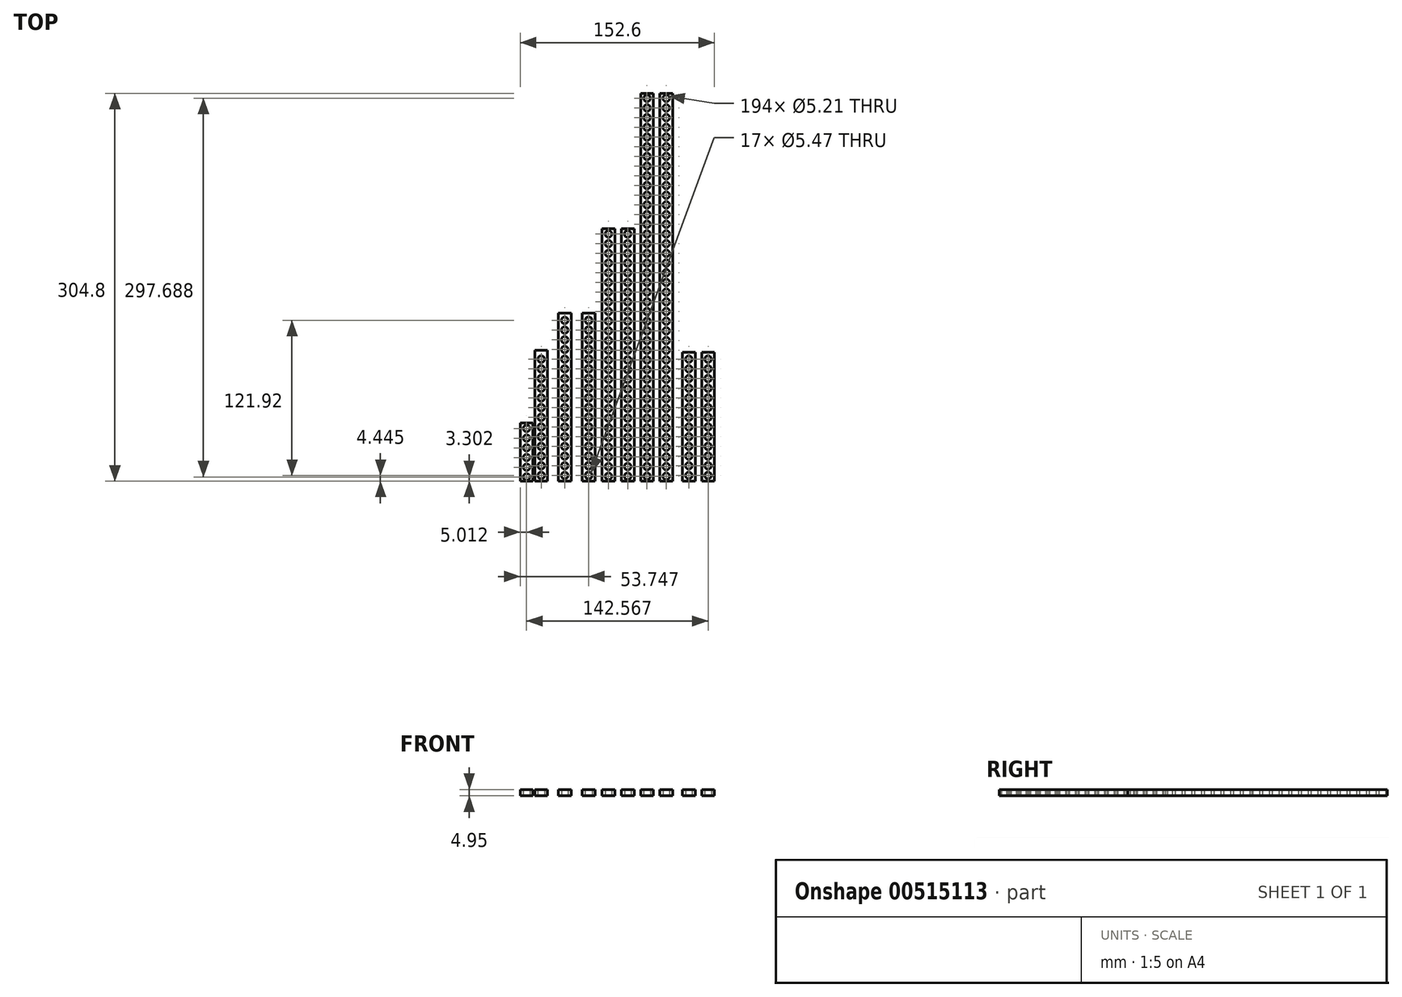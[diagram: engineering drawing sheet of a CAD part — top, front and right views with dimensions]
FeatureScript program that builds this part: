
annotation { "Feature Type Name" : "Feature", "Feature Type Description" : "" }
export const myFeature = defineFeature(function(context is Context, id is Id, definition is map)
    precondition{}
    {
        {
            var Q0;
            Q0=qCreatedBy(makeId("Top.planeOp"),FACE);
            var sketch = newSketch(context, id + "F0", { "sketchPlane" : qUnion([Q0])});
            skLineSegment(sketch, "E0.bottom", {"start": v(-63.67, 0) * mm, "end": v(-53.64, 0) * mm});
            skLineSegment(sketch, "E0.top", {"start": v(-63.67, 102.87) * mm, "end": v(-53.64, 102.87) * mm});
            skLineSegment(sketch, "E0.left", {"start": v(-63.67, 0) * mm, "end": v(-63.67, 102.87) * mm});
            skLineSegment(sketch, "E0.right", {"start": v(-53.64, 0) * mm, "end": v(-53.64, 102.87) * mm});
            skCircle(sketch, "E1", {"center": v(-58.66, 4.45) * mm, "radius": 2.6 * mm});
            skPoint(sketch, "E1.centerSnap0", {"position": v(-58.66, 0) * mm});
            skCircle(sketch, "E2.0.1.0", {"center": v(-58.66, 12.06) * mm, "radius": 2.6 * mm});
            skCircle(sketch, "E2.0.2.0", {"center": v(-58.66, 19.69) * mm, "radius": 2.6 * mm});
            skCircle(sketch, "E2.0.3.0", {"center": v(-58.66, 27.3) * mm, "radius": 2.6 * mm});
            skCircle(sketch, "E2.0.4.0", {"center": v(-58.66, 34.92) * mm, "radius": 2.6 * mm});
            skCircle(sketch, "E2.0.5.0", {"center": v(-58.66, 42.55) * mm, "radius": 2.6 * mm});
            skCircle(sketch, "E2.0.6.0", {"center": v(-58.66, 50.16) * mm, "radius": 2.6 * mm});
            skCircle(sketch, "E2.0.7.0", {"center": v(-58.66, 57.78) * mm, "radius": 2.6 * mm});
            skCircle(sketch, "E2.0.8.0", {"center": v(-58.66, 65.4) * mm, "radius": 2.6 * mm});
            skCircle(sketch, "E2.0.9.0", {"center": v(-58.66, 73.03) * mm, "radius": 2.6 * mm});
            skCircle(sketch, "E2.0.10.0", {"center": v(-58.66, 80.65) * mm, "radius": 2.6 * mm});
            skCircle(sketch, "E2.0.11.0", {"center": v(-58.66, 88.27) * mm, "radius": 2.6 * mm});
            skCircle(sketch, "E2.0.12.0", {"center": v(-58.66, 95.88) * mm, "radius": 2.6 * mm});
            skLineSegment(sketch, "E2.direction1", {"start": v(-58.66, 4.44) * mm, "end": v(-33.26, 4.45) * mm, "construction": true});
            skLineSegment(sketch, "E2.direction2", {"start": v(-58.66, 4.45) * mm, "end": v(-58.66, 12.06) * mm, "construction": true});
            skSolve(sketch);
        }
        {
            var Q0;
            Q0=makeQuery(id+"F0.imprint","IMPRINT",FACE,{"disambiguationData":[TD([[makeQuery(id+"F0.imprint","IMPRINT",EDGE,{"derivedFrom":sQuery(id+"F0.wireOp",EDGE,"E0.bottom")}),1.0]])]});
            extrude(context, id + "F1", {"entities" : qUnion([Q0]), "depth" : 4.95 * mm, "offsetDistance" : 25.4 * mm});
        }
        {
            var Q0;
            Q0=qCreatedBy(makeId("Top.planeOp"),FACE);
            var sketch = newSketch(context, id + "F2", { "sketchPlane" : qUnion([Q0])});
            skLineSegment(sketch, "E3.bottom", {"start": v(-45.23, 0) * mm, "end": v(-35.2, 0) * mm});
            skLineSegment(sketch, "E3.top", {"start": v(-45.23, 132.08) * mm, "end": v(-35.2, 132.08) * mm});
            skLineSegment(sketch, "E3.left", {"start": v(-45.23, 0) * mm, "end": v(-45.23, 132.08) * mm});
            skLineSegment(sketch, "E3.right", {"start": v(-35.2, 0) * mm, "end": v(-35.2, 132.08) * mm});
            skCircle(sketch, "E4", {"center": v(-40.2, 4.44) * mm, "radius": 2.6 * mm});
            skPoint(sketch, "E4.centerSnap0", {"position": v(-40.2, 0) * mm});
            skCircle(sketch, "E5.0.1.0", {"center": v(-40.2, 12.06) * mm, "radius": 2.6 * mm});
            skCircle(sketch, "E5.0.2.0", {"center": v(-40.2, 19.69) * mm, "radius": 2.6 * mm});
            skCircle(sketch, "E5.0.3.0", {"center": v(-40.2, 27.3) * mm, "radius": 2.6 * mm});
            skCircle(sketch, "E5.0.4.0", {"center": v(-40.2, 34.92) * mm, "radius": 2.6 * mm});
            skCircle(sketch, "E5.0.5.0", {"center": v(-40.2, 42.55) * mm, "radius": 2.6 * mm});
            skCircle(sketch, "E5.0.6.0", {"center": v(-40.2, 50.16) * mm, "radius": 2.6 * mm});
            skCircle(sketch, "E5.0.7.0", {"center": v(-40.2, 57.78) * mm, "radius": 2.6 * mm});
            skCircle(sketch, "E5.0.8.0", {"center": v(-40.2, 65.4) * mm, "radius": 2.6 * mm});
            skCircle(sketch, "E5.0.9.0", {"center": v(-40.2, 73.03) * mm, "radius": 2.6 * mm});
            skCircle(sketch, "E5.0.10.0", {"center": v(-40.2, 80.65) * mm, "radius": 2.6 * mm});
            skCircle(sketch, "E5.0.11.0", {"center": v(-40.2, 88.27) * mm, "radius": 2.6 * mm});
            skCircle(sketch, "E5.0.12.0", {"center": v(-40.2, 95.88) * mm, "radius": 2.6 * mm});
            skCircle(sketch, "E5.0.13.0", {"center": v(-40.2, 103.5) * mm, "radius": 2.6 * mm});
            skCircle(sketch, "E5.0.14.0", {"center": v(-40.2, 111.12) * mm, "radius": 2.6 * mm});
            skCircle(sketch, "E5.0.15.0", {"center": v(-40.2, 118.75) * mm, "radius": 2.6 * mm});
            skCircle(sketch, "E5.0.16.0", {"center": v(-40.2, 126.37) * mm, "radius": 2.6 * mm});
            skLineSegment(sketch, "E5.direction1", {"start": v(-40.2, 4.44) * mm, "end": v(-14.8, 4.45) * mm, "construction": true});
            skLineSegment(sketch, "E5.direction2", {"start": v(-40.2, 4.44) * mm, "end": v(-40.2, 12.06) * mm, "construction": true});
            skSolve(sketch);
        }
        {
            var Q0;
            Q0=makeQuery(id+"F2.imprint","IMPRINT",FACE,{"disambiguationData":[TD([[makeQuery(id+"F2.imprint","IMPRINT",EDGE,{"derivedFrom":sQuery(id+"F2.wireOp",EDGE,"E3.bottom")}),1.0]])]});
            extrude(context, id + "F3", {"entities" : qUnion([Q0]), "depth" : 4.95 * mm, "offsetDistance" : 25.4 * mm});
        }
        {
            var Q0;
            Q0=qCreatedBy(makeId("Top.planeOp"),FACE);
            var sketch = newSketch(context, id + "F4", { "sketchPlane" : qUnion([Q0])});
            skLineSegment(sketch, "E6.bottom", {"start": v(-26.44, 0) * mm, "end": v(-16.4, 0) * mm});
            skLineSegment(sketch, "E6.top", {"start": v(-26.44, 132.08) * mm, "end": v(-16.4, 132.08) * mm});
            skLineSegment(sketch, "E6.left", {"start": v(-26.44, 0) * mm, "end": v(-26.44, 132.08) * mm});
            skLineSegment(sketch, "E6.right", {"start": v(-16.4, 0) * mm, "end": v(-16.4, 132.08) * mm});
            skCircle(sketch, "E7", {"center": v(-21.42, 4.45) * mm, "radius": 2.73 * mm});
            skPoint(sketch, "E7.centerSnap0", {"position": v(-21.42, 0) * mm});
            skCircle(sketch, "E8.0.1.0", {"center": v(-21.42, 12.06) * mm, "radius": 2.73 * mm});
            skCircle(sketch, "E8.0.2.0", {"center": v(-21.42, 19.69) * mm, "radius": 2.73 * mm});
            skCircle(sketch, "E8.0.3.0", {"center": v(-21.42, 27.3) * mm, "radius": 2.73 * mm});
            skCircle(sketch, "E8.0.4.0", {"center": v(-21.42, 34.92) * mm, "radius": 2.73 * mm});
            skCircle(sketch, "E8.0.5.0", {"center": v(-21.42, 42.55) * mm, "radius": 2.73 * mm});
            skCircle(sketch, "E8.0.6.0", {"center": v(-21.42, 50.16) * mm, "radius": 2.73 * mm});
            skCircle(sketch, "E8.0.7.0", {"center": v(-21.42, 57.78) * mm, "radius": 2.73 * mm});
            skCircle(sketch, "E8.0.8.0", {"center": v(-21.42, 65.4) * mm, "radius": 2.73 * mm});
            skCircle(sketch, "E8.0.9.0", {"center": v(-21.42, 73.03) * mm, "radius": 2.73 * mm});
            skCircle(sketch, "E8.0.10.0", {"center": v(-21.42, 80.65) * mm, "radius": 2.73 * mm});
            skCircle(sketch, "E8.0.11.0", {"center": v(-21.42, 88.27) * mm, "radius": 2.73 * mm});
            skCircle(sketch, "E8.0.12.0", {"center": v(-21.42, 95.88) * mm, "radius": 2.73 * mm});
            skCircle(sketch, "E8.0.13.0", {"center": v(-21.42, 103.5) * mm, "radius": 2.73 * mm});
            skCircle(sketch, "E8.0.14.0", {"center": v(-21.42, 111.12) * mm, "radius": 2.73 * mm});
            skCircle(sketch, "E8.0.15.0", {"center": v(-21.42, 118.75) * mm, "radius": 2.73 * mm});
            skCircle(sketch, "E8.0.16.0", {"center": v(-21.42, 126.37) * mm, "radius": 2.73 * mm});
            skLineSegment(sketch, "E8.direction1", {"start": v(-21.42, 4.45) * mm, "end": v(3.98, 4.45) * mm, "construction": true});
            skLineSegment(sketch, "E8.direction2", {"start": v(-21.42, 4.45) * mm, "end": v(-21.42, 12.06) * mm, "construction": true});
            skSolve(sketch);
        }
        {
            var Q0;
            Q0=makeQuery(id+"F4.imprint","IMPRINT",FACE,{"disambiguationData":[TD([[makeQuery(id+"F4.imprint","IMPRINT",EDGE,{"derivedFrom":sQuery(id+"F4.wireOp",EDGE,"E6.bottom")}),1.0]])]});
            extrude(context, id + "F5", {"entities" : qUnion([Q0]), "depth" : 4.95 * mm, "offsetDistance" : 25.4 * mm});
        }
        {
            var Q0;
            Q0=qCreatedBy(makeId("Top.planeOp"),FACE);
            var sketch = newSketch(context, id + "F6", { "sketchPlane" : qUnion([Q0])});
            skLineSegment(sketch, "E9.bottom", {"start": v(-10.83, 0) * mm, "end": v(-0.8, 0) * mm});
            skLineSegment(sketch, "E9.top", {"start": v(-10.83, 198.44) * mm, "end": v(-0.8, 198.44) * mm});
            skLineSegment(sketch, "E9.left", {"start": v(-10.83, 0) * mm, "end": v(-10.83, 198.44) * mm});
            skLineSegment(sketch, "E9.right", {"start": v(-0.8, 0) * mm, "end": v(-0.8, 198.44) * mm});
            skLineSegment(sketch, "E10.bottom", {"start": v(4.28, 0) * mm, "end": v(14.32, 0) * mm});
            skLineSegment(sketch, "E10.top", {"start": v(4.28, 198.44) * mm, "end": v(14.32, 198.44) * mm});
            skLineSegment(sketch, "E10.left", {"start": v(4.28, 0) * mm, "end": v(4.28, 198.44) * mm});
            skLineSegment(sketch, "E10.right", {"start": v(14.32, 0) * mm, "end": v(14.32, 198.44) * mm});
            skCircle(sketch, "E11", {"center": v(-5.81, 3.81) * mm, "radius": 2.6 * mm});
            skPoint(sketch, "E11.centerSnap0", {"position": v(-5.81, 0) * mm});
            skCircle(sketch, "E12.0.1.0", {"center": v(-5.81, 11.43) * mm, "radius": 2.6 * mm});
            skCircle(sketch, "E12.0.2.0", {"center": v(-5.81, 19.05) * mm, "radius": 2.6 * mm});
            skCircle(sketch, "E12.0.3.0", {"center": v(-5.81, 26.67) * mm, "radius": 2.6 * mm});
            skCircle(sketch, "E12.0.4.0", {"center": v(-5.81, 34.3) * mm, "radius": 2.6 * mm});
            skCircle(sketch, "E12.0.5.0", {"center": v(-5.81, 41.91) * mm, "radius": 2.6 * mm});
            skCircle(sketch, "E12.0.6.0", {"center": v(-5.81, 49.53) * mm, "radius": 2.6 * mm});
            skCircle(sketch, "E12.0.7.0", {"center": v(-5.81, 57.15) * mm, "radius": 2.6 * mm});
            skCircle(sketch, "E12.0.8.0", {"center": v(-5.81, 64.77) * mm, "radius": 2.6 * mm});
            skCircle(sketch, "E12.0.9.0", {"center": v(-5.81, 72.39) * mm, "radius": 2.6 * mm});
            skCircle(sketch, "E12.0.10.0", {"center": v(-5.81, 80) * mm, "radius": 2.6 * mm});
            skCircle(sketch, "E12.0.11.0", {"center": v(-5.81, 87.63) * mm, "radius": 2.6 * mm});
            skCircle(sketch, "E12.0.12.0", {"center": v(-5.81, 95.25) * mm, "radius": 2.6 * mm});
            skCircle(sketch, "E12.0.13.0", {"center": v(-5.81, 102.87) * mm, "radius": 2.6 * mm});
            skCircle(sketch, "E12.0.14.0", {"center": v(-5.81, 110.49) * mm, "radius": 2.6 * mm});
            skCircle(sketch, "E12.0.15.0", {"center": v(-5.81, 118.11) * mm, "radius": 2.6 * mm});
            skCircle(sketch, "E12.0.16.0", {"center": v(-5.81, 125.73) * mm, "radius": 2.6 * mm});
            skCircle(sketch, "E12.0.17.0", {"center": v(-5.81, 133.35) * mm, "radius": 2.6 * mm});
            skCircle(sketch, "E12.0.18.0", {"center": v(-5.81, 140.97) * mm, "radius": 2.6 * mm});
            skCircle(sketch, "E12.0.19.0", {"center": v(-5.81, 148.6) * mm, "radius": 2.6 * mm});
            skCircle(sketch, "E12.0.20.0", {"center": v(-5.81, 156.21) * mm, "radius": 2.6 * mm});
            skCircle(sketch, "E12.0.21.0", {"center": v(-5.81, 163.83) * mm, "radius": 2.6 * mm});
            skCircle(sketch, "E12.0.22.0", {"center": v(-5.81, 171.45) * mm, "radius": 2.6 * mm});
            skCircle(sketch, "E12.0.23.0", {"center": v(-5.81, 179.07) * mm, "radius": 2.6 * mm});
            skCircle(sketch, "E12.0.24.0", {"center": v(-5.81, 186.7) * mm, "radius": 2.6 * mm});
            skCircle(sketch, "E12.0.25.0", {"center": v(-5.81, 194.3) * mm, "radius": 2.6 * mm});
            skCircle(sketch, "E12.1.0.0", {"center": v(9.3, 3.81) * mm, "radius": 2.6 * mm});
            skCircle(sketch, "E12.1.1.0", {"center": v(9.3, 11.43) * mm, "radius": 2.6 * mm});
            skCircle(sketch, "E12.1.2.0", {"center": v(9.3, 19.05) * mm, "radius": 2.6 * mm});
            skCircle(sketch, "E12.1.3.0", {"center": v(9.3, 26.67) * mm, "radius": 2.6 * mm});
            skCircle(sketch, "E12.1.4.0", {"center": v(9.3, 34.3) * mm, "radius": 2.6 * mm});
            skCircle(sketch, "E12.1.5.0", {"center": v(9.3, 41.91) * mm, "radius": 2.6 * mm});
            skCircle(sketch, "E12.1.6.0", {"center": v(9.3, 49.53) * mm, "radius": 2.6 * mm});
            skCircle(sketch, "E12.1.7.0", {"center": v(9.3, 57.15) * mm, "radius": 2.6 * mm});
            skCircle(sketch, "E12.1.8.0", {"center": v(9.3, 64.77) * mm, "radius": 2.6 * mm});
            skCircle(sketch, "E12.1.9.0", {"center": v(9.3, 72.39) * mm, "radius": 2.6 * mm});
            skCircle(sketch, "E12.1.10.0", {"center": v(9.3, 80) * mm, "radius": 2.6 * mm});
            skCircle(sketch, "E12.1.11.0", {"center": v(9.3, 87.63) * mm, "radius": 2.6 * mm});
            skCircle(sketch, "E12.1.12.0", {"center": v(9.3, 95.25) * mm, "radius": 2.6 * mm});
            skCircle(sketch, "E12.1.13.0", {"center": v(9.3, 102.87) * mm, "radius": 2.6 * mm});
            skCircle(sketch, "E12.1.14.0", {"center": v(9.3, 110.49) * mm, "radius": 2.6 * mm});
            skCircle(sketch, "E12.1.15.0", {"center": v(9.3, 118.11) * mm, "radius": 2.6 * mm});
            skCircle(sketch, "E12.1.16.0", {"center": v(9.3, 125.73) * mm, "radius": 2.6 * mm});
            skCircle(sketch, "E12.1.17.0", {"center": v(9.3, 133.35) * mm, "radius": 2.6 * mm});
            skCircle(sketch, "E12.1.18.0", {"center": v(9.3, 140.97) * mm, "radius": 2.6 * mm});
            skCircle(sketch, "E12.1.19.0", {"center": v(9.3, 148.6) * mm, "radius": 2.6 * mm});
            skCircle(sketch, "E12.1.20.0", {"center": v(9.3, 156.21) * mm, "radius": 2.6 * mm});
            skCircle(sketch, "E12.1.21.0", {"center": v(9.3, 163.83) * mm, "radius": 2.6 * mm});
            skCircle(sketch, "E12.1.22.0", {"center": v(9.3, 171.45) * mm, "radius": 2.6 * mm});
            skCircle(sketch, "E12.1.23.0", {"center": v(9.3, 179.07) * mm, "radius": 2.6 * mm});
            skCircle(sketch, "E12.1.24.0", {"center": v(9.3, 186.7) * mm, "radius": 2.6 * mm});
            skCircle(sketch, "E12.1.25.0", {"center": v(9.3, 194.3) * mm, "radius": 2.6 * mm});
            skLineSegment(sketch, "E12.direction1", {"start": v(-5.81, 3.81) * mm, "end": v(9.3, 3.81) * mm, "construction": true});
            skLineSegment(sketch, "E12.direction2", {"start": v(-5.81, 3.81) * mm, "end": v(-5.81, 11.43) * mm, "construction": true});
            skSolve(sketch);
        }
        {
            var Q0;
            Q0=makeQuery(id+"F6.imprint","IMPRINT",FACE,{"disambiguationData":[TD([[makeQuery(id+"F6.imprint","IMPRINT",EDGE,{"derivedFrom":sQuery(id+"F6.wireOp",EDGE,"E9.bottom")}),1.0]])]});
            var Q1;
            Q1=makeQuery(id+"F6.imprint","IMPRINT",FACE,{"disambiguationData":[TD([[makeQuery(id+"F6.imprint","IMPRINT",EDGE,{"derivedFrom":sQuery(id+"F6.wireOp",EDGE,"E10.bottom")}),1.0]])]});
            extrude(context, id + "F7", {"entities" : qUnion([Q0, Q1]), "depth" : 4.95 * mm, "offsetDistance" : 25.4 * mm});
        }
        {
            var Q0;
            Q0=qCreatedBy(makeId("Top.planeOp"),FACE);
            var sketch = newSketch(context, id + "F8", { "sketchPlane" : qUnion([Q0])});
            skLineSegment(sketch, "E13.bottom", {"start": v(19.42, 0) * mm, "end": v(29.46, 0) * mm});
            skLineSegment(sketch, "E13.top", {"start": v(19.42, 304.8) * mm, "end": v(29.46, 304.8) * mm});
            skLineSegment(sketch, "E13.left", {"start": v(19.42, 0) * mm, "end": v(19.42, 304.8) * mm});
            skLineSegment(sketch, "E13.right", {"start": v(29.46, 0) * mm, "end": v(29.46, 304.8) * mm});
            skCircle(sketch, "E14", {"center": v(24.44, 3.81) * mm, "radius": 2.6 * mm});
            skPoint(sketch, "E14.centerSnap0", {"position": v(24.44, 0) * mm});
            skLineSegment(sketch, "E15.bottom", {"start": v(34.54, 0) * mm, "end": v(44.57, 0) * mm});
            skLineSegment(sketch, "E15.top", {"start": v(34.54, 304.8) * mm, "end": v(44.57, 304.8) * mm});
            skLineSegment(sketch, "E15.left", {"start": v(34.54, 0) * mm, "end": v(34.54, 304.8) * mm});
            skLineSegment(sketch, "E15.right", {"start": v(44.57, 0) * mm, "end": v(44.57, 304.8) * mm});
            skCircle(sketch, "E16.0.1.0", {"center": v(24.44, 11.43) * mm, "radius": 2.6 * mm});
            skCircle(sketch, "E16.0.2.0", {"center": v(24.44, 19.05) * mm, "radius": 2.6 * mm});
            skCircle(sketch, "E16.0.3.0", {"center": v(24.44, 26.67) * mm, "radius": 2.6 * mm});
            skCircle(sketch, "E16.0.4.0", {"center": v(24.44, 34.3) * mm, "radius": 2.6 * mm});
            skCircle(sketch, "E16.0.5.0", {"center": v(24.44, 41.91) * mm, "radius": 2.6 * mm});
            skCircle(sketch, "E16.0.6.0", {"center": v(24.44, 49.53) * mm, "radius": 2.6 * mm});
            skCircle(sketch, "E16.0.7.0", {"center": v(24.44, 57.15) * mm, "radius": 2.6 * mm});
            skCircle(sketch, "E16.0.8.0", {"center": v(24.44, 64.77) * mm, "radius": 2.6 * mm});
            skCircle(sketch, "E16.0.9.0", {"center": v(24.44, 72.4) * mm, "radius": 2.6 * mm});
            skCircle(sketch, "E16.0.10.0", {"center": v(24.44, 80) * mm, "radius": 2.6 * mm});
            skCircle(sketch, "E16.0.11.0", {"center": v(24.44, 87.63) * mm, "radius": 2.6 * mm});
            skCircle(sketch, "E16.0.12.0", {"center": v(24.44, 95.25) * mm, "radius": 2.6 * mm});
            skCircle(sketch, "E16.0.13.0", {"center": v(24.44, 102.87) * mm, "radius": 2.6 * mm});
            skCircle(sketch, "E16.0.14.0", {"center": v(24.44, 110.5) * mm, "radius": 2.6 * mm});
            skCircle(sketch, "E16.0.15.0", {"center": v(24.44, 118.11) * mm, "radius": 2.6 * mm});
            skCircle(sketch, "E16.0.16.0", {"center": v(24.44, 125.73) * mm, "radius": 2.6 * mm});
            skCircle(sketch, "E16.0.17.0", {"center": v(24.44, 133.35) * mm, "radius": 2.6 * mm});
            skCircle(sketch, "E16.0.18.0", {"center": v(24.44, 140.97) * mm, "radius": 2.6 * mm});
            skCircle(sketch, "E16.0.19.0", {"center": v(24.44, 148.6) * mm, "radius": 2.6 * mm});
            skCircle(sketch, "E16.0.20.0", {"center": v(24.44, 156.21) * mm, "radius": 2.6 * mm});
            skCircle(sketch, "E16.0.21.0", {"center": v(24.44, 163.83) * mm, "radius": 2.6 * mm});
            skCircle(sketch, "E16.0.22.0", {"center": v(24.44, 171.45) * mm, "radius": 2.6 * mm});
            skCircle(sketch, "E16.0.23.0", {"center": v(24.44, 179.07) * mm, "radius": 2.6 * mm});
            skCircle(sketch, "E16.0.24.0", {"center": v(24.44, 186.7) * mm, "radius": 2.6 * mm});
            skCircle(sketch, "E16.0.25.0", {"center": v(24.44, 194.3) * mm, "radius": 2.6 * mm});
            skCircle(sketch, "E16.0.26.0", {"center": v(24.44, 201.93) * mm, "radius": 2.6 * mm});
            skCircle(sketch, "E16.0.27.0", {"center": v(24.44, 209.55) * mm, "radius": 2.6 * mm});
            skCircle(sketch, "E16.0.28.0", {"center": v(24.44, 217.17) * mm, "radius": 2.6 * mm});
            skCircle(sketch, "E16.0.29.0", {"center": v(24.44, 224.8) * mm, "radius": 2.6 * mm});
            skCircle(sketch, "E16.0.30.0", {"center": v(24.44, 232.4) * mm, "radius": 2.6 * mm});
            skCircle(sketch, "E16.0.31.0", {"center": v(24.44, 240.03) * mm, "radius": 2.6 * mm});
            skCircle(sketch, "E16.0.32.0", {"center": v(24.44, 247.65) * mm, "radius": 2.6 * mm});
            skCircle(sketch, "E16.0.33.0", {"center": v(24.44, 255.27) * mm, "radius": 2.6 * mm});
            skCircle(sketch, "E16.0.34.0", {"center": v(24.44, 262.89) * mm, "radius": 2.6 * mm});
            skCircle(sketch, "E16.0.35.0", {"center": v(24.44, 270.5) * mm, "radius": 2.6 * mm});
            skCircle(sketch, "E16.0.36.0", {"center": v(24.44, 278.13) * mm, "radius": 2.6 * mm});
            skCircle(sketch, "E16.0.37.0", {"center": v(24.44, 285.75) * mm, "radius": 2.6 * mm});
            skCircle(sketch, "E16.0.38.0", {"center": v(24.44, 293.37) * mm, "radius": 2.6 * mm});
            skCircle(sketch, "E16.0.39.0", {"center": v(24.44, 300.99) * mm, "radius": 2.6 * mm});
            skCircle(sketch, "E16.1.0.0", {"center": v(39.55, 3.81) * mm, "radius": 2.6 * mm});
            skCircle(sketch, "E16.1.1.0", {"center": v(39.55, 11.43) * mm, "radius": 2.6 * mm});
            skCircle(sketch, "E16.1.2.0", {"center": v(39.55, 19.05) * mm, "radius": 2.6 * mm});
            skCircle(sketch, "E16.1.3.0", {"center": v(39.55, 26.67) * mm, "radius": 2.6 * mm});
            skCircle(sketch, "E16.1.4.0", {"center": v(39.55, 34.3) * mm, "radius": 2.6 * mm});
            skCircle(sketch, "E16.1.5.0", {"center": v(39.55, 41.91) * mm, "radius": 2.6 * mm});
            skCircle(sketch, "E16.1.6.0", {"center": v(39.55, 49.53) * mm, "radius": 2.6 * mm});
            skCircle(sketch, "E16.1.7.0", {"center": v(39.55, 57.15) * mm, "radius": 2.6 * mm});
            skCircle(sketch, "E16.1.8.0", {"center": v(39.55, 64.77) * mm, "radius": 2.6 * mm});
            skCircle(sketch, "E16.1.9.0", {"center": v(39.55, 72.4) * mm, "radius": 2.6 * mm});
            skCircle(sketch, "E16.1.10.0", {"center": v(39.55, 80) * mm, "radius": 2.6 * mm});
            skCircle(sketch, "E16.1.11.0", {"center": v(39.55, 87.63) * mm, "radius": 2.6 * mm});
            skCircle(sketch, "E16.1.12.0", {"center": v(39.55, 95.25) * mm, "radius": 2.6 * mm});
            skCircle(sketch, "E16.1.13.0", {"center": v(39.55, 102.87) * mm, "radius": 2.6 * mm});
            skCircle(sketch, "E16.1.14.0", {"center": v(39.55, 110.5) * mm, "radius": 2.6 * mm});
            skCircle(sketch, "E16.1.15.0", {"center": v(39.55, 118.11) * mm, "radius": 2.6 * mm});
            skCircle(sketch, "E16.1.16.0", {"center": v(39.55, 125.73) * mm, "radius": 2.6 * mm});
            skCircle(sketch, "E16.1.17.0", {"center": v(39.55, 133.35) * mm, "radius": 2.6 * mm});
            skCircle(sketch, "E16.1.18.0", {"center": v(39.55, 140.97) * mm, "radius": 2.6 * mm});
            skCircle(sketch, "E16.1.19.0", {"center": v(39.55, 148.6) * mm, "radius": 2.6 * mm});
            skCircle(sketch, "E16.1.20.0", {"center": v(39.55, 156.21) * mm, "radius": 2.6 * mm});
            skCircle(sketch, "E16.1.21.0", {"center": v(39.55, 163.83) * mm, "radius": 2.6 * mm});
            skCircle(sketch, "E16.1.22.0", {"center": v(39.55, 171.45) * mm, "radius": 2.6 * mm});
            skCircle(sketch, "E16.1.23.0", {"center": v(39.55, 179.07) * mm, "radius": 2.6 * mm});
            skCircle(sketch, "E16.1.24.0", {"center": v(39.55, 186.7) * mm, "radius": 2.6 * mm});
            skCircle(sketch, "E16.1.25.0", {"center": v(39.55, 194.3) * mm, "radius": 2.6 * mm});
            skCircle(sketch, "E16.1.26.0", {"center": v(39.55, 201.93) * mm, "radius": 2.6 * mm});
            skCircle(sketch, "E16.1.27.0", {"center": v(39.55, 209.55) * mm, "radius": 2.6 * mm});
            skCircle(sketch, "E16.1.28.0", {"center": v(39.55, 217.17) * mm, "radius": 2.6 * mm});
            skCircle(sketch, "E16.1.29.0", {"center": v(39.55, 224.8) * mm, "radius": 2.6 * mm});
            skCircle(sketch, "E16.1.30.0", {"center": v(39.55, 232.4) * mm, "radius": 2.6 * mm});
            skCircle(sketch, "E16.1.31.0", {"center": v(39.55, 240.03) * mm, "radius": 2.6 * mm});
            skCircle(sketch, "E16.1.32.0", {"center": v(39.55, 247.65) * mm, "radius": 2.6 * mm});
            skCircle(sketch, "E16.1.33.0", {"center": v(39.55, 255.27) * mm, "radius": 2.6 * mm});
            skCircle(sketch, "E16.1.34.0", {"center": v(39.55, 262.89) * mm, "radius": 2.6 * mm});
            skCircle(sketch, "E16.1.35.0", {"center": v(39.55, 270.5) * mm, "radius": 2.6 * mm});
            skCircle(sketch, "E16.1.36.0", {"center": v(39.55, 278.13) * mm, "radius": 2.6 * mm});
            skCircle(sketch, "E16.1.37.0", {"center": v(39.55, 285.75) * mm, "radius": 2.6 * mm});
            skCircle(sketch, "E16.1.38.0", {"center": v(39.55, 293.37) * mm, "radius": 2.6 * mm});
            skCircle(sketch, "E16.1.39.0", {"center": v(39.55, 300.99) * mm, "radius": 2.6 * mm});
            skLineSegment(sketch, "E16.direction1", {"start": v(24.44, 3.81) * mm, "end": v(39.55, 3.81) * mm, "construction": true});
            skLineSegment(sketch, "E16.direction2", {"start": v(24.44, 3.81) * mm, "end": v(24.44, 11.43) * mm, "construction": true});
            skSolve(sketch);
        }
        {
            var Q0;
            Q0=makeQuery(id+"F8.imprint","IMPRINT",FACE,{"disambiguationData":[TD([[makeQuery(id+"F8.imprint","IMPRINT",EDGE,{"derivedFrom":sQuery(id+"F8.wireOp",EDGE,"E13.bottom")}),1.0]])]});
            var Q1;
            Q1=makeQuery(id+"F8.imprint","IMPRINT",FACE,{"disambiguationData":[TD([[makeQuery(id+"F8.imprint","IMPRINT",EDGE,{"derivedFrom":sQuery(id+"F8.wireOp",EDGE,"E15.bottom")}),1.0]])]});
            extrude(context, id + "F9", {"entities" : qUnion([Q0, Q1]), "depth" : 4.95 * mm, "offsetDistance" : 25.4 * mm});
        }
        {
            var Q0;
            Q0=qCreatedBy(makeId("Top.planeOp"),FACE);
            var sketch = newSketch(context, id + "F10", { "sketchPlane" : qUnion([Q0])});
            skLineSegment(sketch, "E17.bottom", {"start": v(52.28, 0) * mm, "end": v(62.31, 0) * mm});
            skLineSegment(sketch, "E17.top", {"start": v(52.28, 101.22) * mm, "end": v(62.31, 101.22) * mm});
            skLineSegment(sketch, "E17.left", {"start": v(52.28, 0) * mm, "end": v(52.28, 101.22) * mm});
            skLineSegment(sketch, "E17.right", {"start": v(62.31, 0) * mm, "end": v(62.31, 101.22) * mm});
            skLineSegment(sketch, "E18.bottom", {"start": v(67.4, 0) * mm, "end": v(77.43, 0) * mm});
            skLineSegment(sketch, "E18.top", {"start": v(67.4, 101.22) * mm, "end": v(77.43, 101.22) * mm});
            skLineSegment(sketch, "E18.left", {"start": v(67.4, 0) * mm, "end": v(67.4, 101.22) * mm});
            skLineSegment(sketch, "E18.right", {"start": v(77.43, 0) * mm, "end": v(77.43, 101.22) * mm});
            skCircle(sketch, "E19", {"center": v(57.3, 4.45) * mm, "radius": 2.6 * mm});
            skPoint(sketch, "E19.centerSnap0", {"position": v(57.3, 0) * mm});
            skCircle(sketch, "E20.0.1.0", {"center": v(57.3, 12.06) * mm, "radius": 2.6 * mm});
            skCircle(sketch, "E20.0.2.0", {"center": v(57.3, 19.69) * mm, "radius": 2.6 * mm});
            skCircle(sketch, "E20.0.3.0", {"center": v(57.3, 27.3) * mm, "radius": 2.6 * mm});
            skCircle(sketch, "E20.0.4.0", {"center": v(57.3, 34.92) * mm, "radius": 2.6 * mm});
            skCircle(sketch, "E20.0.5.0", {"center": v(57.3, 42.55) * mm, "radius": 2.6 * mm});
            skCircle(sketch, "E20.0.6.0", {"center": v(57.3, 50.16) * mm, "radius": 2.6 * mm});
            skCircle(sketch, "E20.0.7.0", {"center": v(57.3, 57.78) * mm, "radius": 2.6 * mm});
            skCircle(sketch, "E20.0.8.0", {"center": v(57.3, 65.4) * mm, "radius": 2.6 * mm});
            skCircle(sketch, "E20.0.9.0", {"center": v(57.3, 73.03) * mm, "radius": 2.6 * mm});
            skCircle(sketch, "E20.0.10.0", {"center": v(57.3, 80.65) * mm, "radius": 2.6 * mm});
            skCircle(sketch, "E20.0.11.0", {"center": v(57.3, 88.27) * mm, "radius": 2.6 * mm});
            skCircle(sketch, "E20.0.12.0", {"center": v(57.3, 95.88) * mm, "radius": 2.6 * mm});
            skCircle(sketch, "E20.1.0.0", {"center": v(72.4, 4.45) * mm, "radius": 2.6 * mm});
            skCircle(sketch, "E20.1.1.0", {"center": v(72.4, 12.06) * mm, "radius": 2.6 * mm});
            skCircle(sketch, "E20.1.2.0", {"center": v(72.4, 19.69) * mm, "radius": 2.6 * mm});
            skCircle(sketch, "E20.1.3.0", {"center": v(72.4, 27.3) * mm, "radius": 2.6 * mm});
            skCircle(sketch, "E20.1.4.0", {"center": v(72.4, 34.92) * mm, "radius": 2.6 * mm});
            skCircle(sketch, "E20.1.5.0", {"center": v(72.4, 42.55) * mm, "radius": 2.6 * mm});
            skCircle(sketch, "E20.1.6.0", {"center": v(72.4, 50.16) * mm, "radius": 2.6 * mm});
            skCircle(sketch, "E20.1.7.0", {"center": v(72.4, 57.78) * mm, "radius": 2.6 * mm});
            skCircle(sketch, "E20.1.8.0", {"center": v(72.4, 65.4) * mm, "radius": 2.6 * mm});
            skCircle(sketch, "E20.1.9.0", {"center": v(72.4, 73.03) * mm, "radius": 2.6 * mm});
            skCircle(sketch, "E20.1.10.0", {"center": v(72.4, 80.65) * mm, "radius": 2.6 * mm});
            skCircle(sketch, "E20.1.11.0", {"center": v(72.4, 88.27) * mm, "radius": 2.6 * mm});
            skCircle(sketch, "E20.1.12.0", {"center": v(72.4, 95.88) * mm, "radius": 2.6 * mm});
            skLineSegment(sketch, "E20.direction1", {"start": v(57.3, 4.45) * mm, "end": v(72.4, 4.45) * mm, "construction": true});
            skLineSegment(sketch, "E20.direction2", {"start": v(57.3, 4.45) * mm, "end": v(57.3, 12.06) * mm, "construction": true});
            skSolve(sketch);
        }
        {
            var Q0;
            Q0=makeQuery(id+"F10.imprint","IMPRINT",FACE,{"disambiguationData":[TD([[makeQuery(id+"F10.imprint","IMPRINT",EDGE,{"derivedFrom":sQuery(id+"F10.wireOp",EDGE,"E17.bottom")}),1.0]])]});
            var Q1;
            Q1=makeQuery(id+"F10.imprint","IMPRINT",FACE,{"disambiguationData":[TD([[makeQuery(id+"F10.imprint","IMPRINT",EDGE,{"derivedFrom":sQuery(id+"F10.wireOp",EDGE,"E18.bottom")}),1.0]])]});
            extrude(context, id + "F11", {"entities" : qUnion([Q0, Q1]), "depth" : 4.95 * mm, "offsetDistance" : 25.4 * mm});
        }
        {
            var Q0;
            Q0=qCreatedBy(makeId("Top.planeOp"),FACE);
            var sketch = newSketch(context, id + "F12", { "sketchPlane" : qUnion([Q0])});
            skLineSegment(sketch, "E21.bottom", {"start": v(-75.17, 0) * mm, "end": v(-65.14, 0) * mm});
            skLineSegment(sketch, "E21.top", {"start": v(-75.17, 45.72) * mm, "end": v(-65.14, 45.72) * mm});
            skLineSegment(sketch, "E21.left", {"start": v(-75.17, 0) * mm, "end": v(-75.17, 45.72) * mm});
            skLineSegment(sketch, "E21.right", {"start": v(-65.14, 0) * mm, "end": v(-65.14, 45.72) * mm});
            skLineSegment(sketch, "E22", {"start": v(-70.16, 0) * mm, "end": v(-70.16, 3.3) * mm, "construction": true});
            skCircle(sketch, "E23", {"center": v(-70.16, 3.3) * mm, "radius": 2.6 * mm});
            skCircle(sketch, "E24.0.1.0", {"center": v(-70.16, 10.92) * mm, "radius": 2.6 * mm});
            skCircle(sketch, "E24.0.2.0", {"center": v(-70.16, 18.54) * mm, "radius": 2.6 * mm});
            skCircle(sketch, "E24.0.3.0", {"center": v(-70.16, 26.16) * mm, "radius": 2.6 * mm});
            skCircle(sketch, "E24.0.4.0", {"center": v(-70.16, 33.78) * mm, "radius": 2.6 * mm});
            skCircle(sketch, "E24.0.5.0", {"center": v(-70.16, 41.4) * mm, "radius": 2.6 * mm});
            skLineSegment(sketch, "E24.direction1", {"start": v(-70.16, 3.3) * mm, "end": v(-44.76, 3.3) * mm, "construction": true});
            skLineSegment(sketch, "E24.direction2", {"start": v(-70.16, 3.3) * mm, "end": v(-70.16, 10.92) * mm, "construction": true});
            skSolve(sketch);
        }
        {
            var Q0;
            Q0=makeQuery(id+"F12.imprint","IMPRINT",FACE,{"disambiguationData":[TD([[makeQuery(id+"F12.imprint","IMPRINT",EDGE,{"derivedFrom":sQuery(id+"F12.wireOp",EDGE,"E21.bottom")}),1.0]])]});
            extrude(context, id + "F13", {"entities" : qUnion([Q0]), "depth" : 4.95 * mm, "offsetDistance" : 25.4 * mm});
        }
    });
